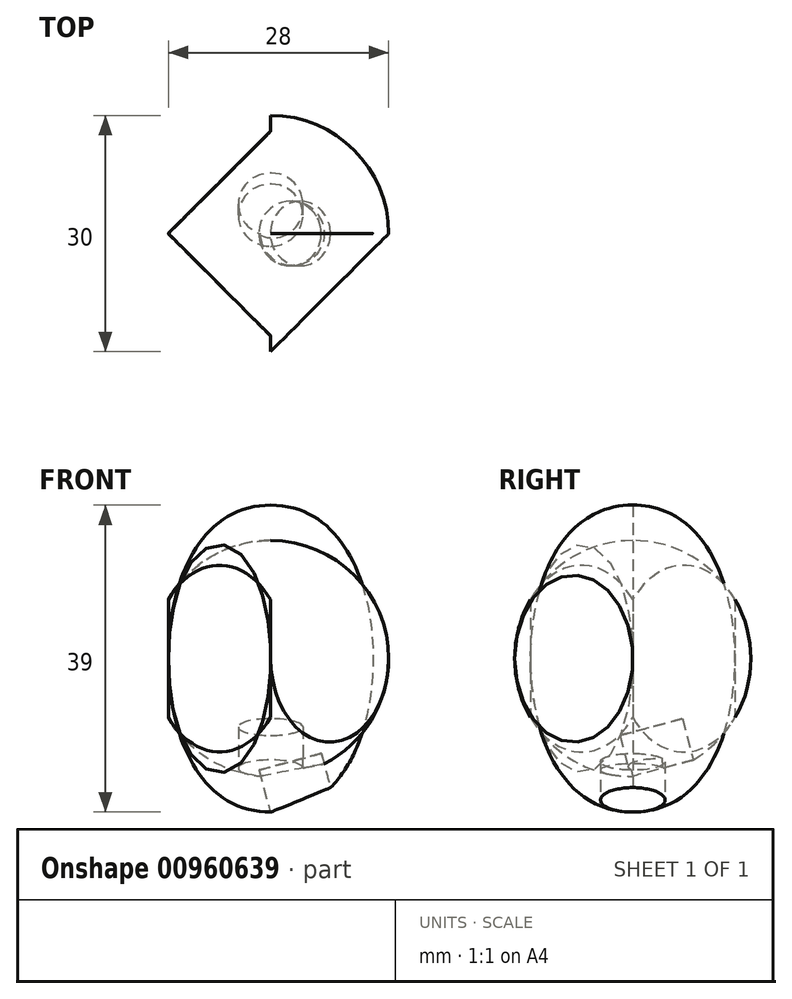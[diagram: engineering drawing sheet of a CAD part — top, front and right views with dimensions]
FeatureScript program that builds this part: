
annotation { "Feature Type Name" : "Feature", "Feature Type Description" : "" }
export const myFeature = defineFeature(function(context is Context, id is Id, definition is map)
    precondition{}
    {
        {
            var Q0;
            Q0=qCreatedBy(makeId("Front.planeOp"),FACE);
            var sketch = newSketch(context, id + "F0", { "sketchPlane" : qUnion([Q0])});
            skArc(sketch, "E0", {"start": v(0, -6) * mm, "mid": v(6, 0) * mm, "end": v(0, 6) * mm});
            skLineSegment(sketch, "E1", {"start": v(0, 6) * mm, "end": v(0, -6) * mm});
            skSolve(sketch);
        }
        {
            var Q0;
            Q0 = qSketchRegion(id + "F0", true);
            var Q1;
            Q1=sQuery(id+"F0.wireOp",EDGE,"E1");
            revolve(context, id + "F1", {"surfaceOperationType" : NewSurfaceOperationType.NEW, "entities" : qUnion([Q0]), "axis" : qUnion([Q1]), "revolveType" : RevolveType.FULL});
        }
        {
            var Q0;
            Q0=qCreatedBy(makeId("Front.planeOp"),FACE);
            var sketch = newSketch(context, id + "F2", { "sketchPlane" : qUnion([Q0])});
            skLineSegment(sketch, "E2", {"start": v(0, 16.05) * mm, "end": v(0, -21.63) * mm, "construction": true});
            skLineSegment(sketch, "E3.bottom", {"start": v(-1, 7.22) * mm, "end": v(1, 7.22) * mm});
            skLineSegment(sketch, "E3.top", {"start": v(-1, -7.38) * mm, "end": v(1, -7.38) * mm});
            skLineSegment(sketch, "E3.left", {"start": v(-1, 7.22) * mm, "end": v(-1, -7.38) * mm});
            skLineSegment(sketch, "E3.right", {"start": v(1, 7.22) * mm, "end": v(1, -7.38) * mm});
            skSolve(sketch);
        }
        {
            var Q0;
            Q0 = qSketchRegion(id + "F2", true);
            extrude(context, id + "F3", {"entities" : qUnion([Q0]), "operationType" : NewBodyOperationType.REMOVE, "endBound" : BoundingType.THROUGH_ALL, "oppositeDirection" : true, "depth" : 25 * mm, "offsetDistance" : 25 * mm, "hasSecondDirection" : true, "secondDirectionOppositeDirection" : false, "secondDirectionDepth" : 25 * mm});
        }
        {
            var Q0;
            Q0=qCreatedBy(makeId("Top.planeOp"),FACE);
            cPlane(context, id + "F4", {"entities" : qUnion([Q0]), "cplaneType" : CPlaneType.OFFSET, "offset" : 6 * mm, "width" : 150 * mm, "height" : 150 * mm});
        }
        {
            var Q0;
            Q0=qCreatedBy(id+"F4.planeOp",FACE);
            var sketch = newSketch(context, id + "F5", { "sketchPlane" : qUnion([Q0])});
            skLineSegment(sketch, "E4", {"start": v(-12.79, 0) * mm, "end": v(12.47, 0) * mm, "construction": true});
            skCircle(sketch, "E5", {"center": v(3.5, 0) * mm, "radius": 1.5 * mm});
            skCircle(sketch, "E6", {"center": v(-3.5, 0) * mm, "radius": 1.5 * mm});
            skSolve(sketch);
        }
        {
            var Q0;
            Q0 = qSketchRegion(id + "F5", true);
            extrude(context, id + "F6", {"entities" : qUnion([Q0]), "operationType" : NewBodyOperationType.REMOVE, "oppositeDirection" : true, "depth" : 6 * mm, "offsetDistance" : 25 * mm});
        }
        {
            var Q0;
            Q0=qCreatedBy(makeId("Front.planeOp"),FACE);
            var sketch = newSketch(context, id + "F7", { "sketchPlane" : qUnion([Q0])});
            skLineSegment(sketch, "E7.bottom", {"start": v(-12.5, 10) * mm, "end": v(12.5, 10) * mm, "construction": true});
            skLineSegment(sketch, "E7.top", {"start": v(-12.5, -10) * mm, "end": v(12.5, -10) * mm, "construction": true});
            skLineSegment(sketch, "E7.left", {"start": v(-12.5, 10) * mm, "end": v(-12.5, -10) * mm, "construction": true});
            skLineSegment(sketch, "E7.right", {"start": v(12.5, 10) * mm, "end": v(12.5, -10) * mm, "construction": true});
            skLineSegment(sketch, "E8", {"start": v(-15.17, 0) * mm, "end": v(15, 0) * mm, "construction": true});
            skPoint(sketch, "E9.snap10", {"position": v(0, 10) * mm});
            skFitSpline(sketch, "E10", {"points": [v(-12.5, 0) * mm, v(0, 10) * mm, v(12.5, 0) * mm], "startDerivative": vector(0, 35.85) * mm, "endDerivative": vector(0, -35.89) * mm});
            skLineSegment(sketch, "E11", {"start": v(-12.5, 0) * mm, "end": v(12.5, 0) * mm});
            skSolve(sketch);
        }
        {
            var Q0;
            Q0 = qSketchRegion(id + "F7", true);
            var Q1;
            Q1=sQuery(id+"F7.wireOp",EDGE,"E11");
            revolve(context, id + "F8", {"surfaceOperationType" : NewSurfaceOperationType.NEW, "entities" : qUnion([Q0]), "axis" : qUnion([Q1]), "revolveType" : RevolveType.FULL});
        }
        {
            var Q0;
            Q0=qCreatedBy(makeId("Front.planeOp"),FACE);
            var sketch = newSketch(context, id + "F9", { "sketchPlane" : qUnion([Q0])});
            skLineSegment(sketch, "E12.bottom", {"start": v(-19.8, 1) * mm, "end": v(19.67, 1) * mm});
            skLineSegment(sketch, "E12.top", {"start": v(-19.8, -1) * mm, "end": v(19.67, -1) * mm});
            skLineSegment(sketch, "E12.left", {"start": v(-19.8, 1) * mm, "end": v(-19.8, -1) * mm});
            skLineSegment(sketch, "E12.right", {"start": v(19.67, 1) * mm, "end": v(19.67, -1) * mm});
            skSolve(sketch);
        }
        {
            var Q0;
            Q0 = qSketchRegion(id + "F9", true);
            extrude(context, id + "F10", {"entities" : qUnion([Q0]), "operationType" : NewBodyOperationType.REMOVE, "endBound" : BoundingType.THROUGH_ALL, "oppositeDirection" : true, "depth" : 25 * mm, "offsetDistance" : 25 * mm, "hasSecondDirection" : true, "secondDirectionOppositeDirection" : false, "secondDirectionDepth" : 25 * mm});
        }
        {
            var Q0;
            Q0=qCreatedBy(makeId("Top.planeOp"),FACE);
            cPlane(context, id + "F11", {"entities" : qUnion([Q0]), "cplaneType" : CPlaneType.OFFSET, "offset" : 10 * mm, "width" : 150 * mm, "height" : 150 * mm});
        }
        {
            var Q0;
            Q0=qCreatedBy(id+"F11.planeOp",FACE);
            var sketch = newSketch(context, id + "F12", { "sketchPlane" : qUnion([Q0])});
            skLineSegment(sketch, "E13", {"start": v(-18, 0) * mm, "end": v(16.68, 0) * mm, "construction": true});
            skCircle(sketch, "E14", {"center": v(-6, 0) * mm, "radius": 1.5 * mm});
            skSolve(sketch);
        }
        {
            var Q0;
            Q0 = qSketchRegion(id + "F12", true);
            extrude(context, id + "F13", {"entities" : qUnion([Q0]), "operationType" : NewBodyOperationType.REMOVE, "oppositeDirection" : true, "depth" : 6 * mm, "offsetDistance" : 25 * mm});
        }
        {
            var Q0;
            Q0=makeQuery(id+"F3.boolean.opBoolean","SPLIT",BODY,{"disambiguationData":[OD(1.0)],"derivedFrom":makeQuery(id+"F1.opRevolve","SWEPT_BODY",BODY,{"disambiguationData":[OSD([sQuery(id+"F0.wireOp",EDGE,"E0"),sQuery(id+"F0.wireOp",EDGE,"E1")])]})});
            deleteBodies(context, id + "F14", {"entities" : qUnion([Q0])});
        }
        {
            var Q0;
            Q0=makeQuery(id+"F10.boolean.opBoolean","SPLIT",BODY,{"disambiguationData":[OD(1.0)],"derivedFrom":makeQuery(id+"F8.opRevolve","SWEPT_BODY",BODY,{"disambiguationData":[OSD([sQuery(id+"F7.wireOp",EDGE,"E10"),sQuery(id+"F7.wireOp",EDGE,"E11")])]})});
            deleteBodies(context, id + "F15", {"entities" : qUnion([Q0])});
        }
        {
            var Q0;
            Q0=qCreatedBy(makeId("Front.planeOp"),FACE);
            var sketch = newSketch(context, id + "F16", { "sketchPlane" : qUnion([Q0])});
            skArc(sketch, "E15", {"start": v(0, -15) * mm, "mid": v(15, 0) * mm, "end": v(0, 15) * mm});
            skLineSegment(sketch, "E16", {"start": v(0, 15) * mm, "end": v(0, -15) * mm});
            skSolve(sketch);
        }
        {
            var Q0;
            Q0 = qSketchRegion(id + "F16", true);
            var Q1;
            Q1=sQuery(id+"F16.wireOp",EDGE,"E16");
            revolve(context, id + "F17", {"surfaceOperationType" : NewSurfaceOperationType.NEW, "entities" : qUnion([Q0]), "axis" : qUnion([Q1]), "revolveType" : RevolveType.FULL});
        }
        {
            var Q0;
            Q0=qCreatedBy(makeId("Top.planeOp"),FACE);
            var sketch = newSketch(context, id + "F18", { "sketchPlane" : qUnion([Q0])});
            skLineSegment(sketch, "E17", {"start": v(0, 171.32) * mm, "end": v(0, -202.95) * mm, "construction": true});
            skLineSegment(sketch, "E18", {"start": v(-199.18, 0) * mm, "end": v(193.35, 0) * mm, "construction": true});
            skCircle(sketch, "E19", {"center": v(0, 0) * mm, "radius": 15 * mm, "construction": true});
            skLineSegment(sketch, "E20", {"start": v(-22.47, 0) * mm, "end": v(-15, 0) * mm});
            skLineSegment(sketch, "E21", {"start": v(-15, 0) * mm, "end": v(0, -15) * mm});
            skLineSegment(sketch, "E22", {"start": v(0, -15) * mm, "end": v(15, 0) * mm});
            skLineSegment(sketch, "E23", {"start": v(15, 0) * mm, "end": v(22.44, 0) * mm});
            skLineSegment(sketch, "E24", {"start": v(22.44, 0) * mm, "end": v(22.44, -21.7) * mm});
            skLineSegment(sketch, "E25", {"start": v(22.44, -21.7) * mm, "end": v(-22.47, -21.7) * mm});
            skLineSegment(sketch, "E26", {"start": v(-22.47, -21.7) * mm, "end": v(-22.47, 0) * mm});
            skSolve(sketch);
        }
        {
            var Q0;
            Q0 = qSketchRegion(id + "F18", true);
            extrude(context, id + "F19", {"entities" : qUnion([Q0]), "operationType" : NewBodyOperationType.REMOVE, "endBound" : BoundingType.THROUGH_ALL, "oppositeDirection" : true, "depth" : 25 * mm, "offsetDistance" : 25 * mm, "hasSecondDirection" : true, "secondDirectionOppositeDirection" : false, "secondDirectionDepth" : 25 * mm});
        }
        {
            var Q0;
            Q0=qCreatedBy(makeId("Right.planeOp"),FACE);
            var sketch = newSketch(context, id + "F20", { "sketchPlane" : qUnion([Q0])});
            skCircle(sketch, "E27", {"center": v(0, 0) * mm, "radius": 15 * mm, "construction": true});
            skLineSegment(sketch, "E28", {"start": v(-19.19, -20.67) * mm, "end": v(25.4, -8.72) * mm, "construction": true});
            skLineSegment(sketch, "E29", {"start": v(36.07, 0) * mm, "end": v(-35.32, 0) * mm, "construction": true});
            skLineSegment(sketch, "E30", {"start": v(0, 0) * mm, "end": v(8.49, -31.68) * mm, "construction": true});
            skSolve(sketch);
        }
        {
            var Q0;
            Q0=sQuery(id+"F20.wireOp",EDGE,"E28");
            cPlane(context, id + "F21", {"entities" : qUnion([Q0]), "cplaneType" : CPlaneType.LINE_ANGLE, "offset" : 25 * mm, "angle" : 0 * degree, "width" : 150 * mm, "height" : 150 * mm});
        }
        {
            var Q0;
            Q0=qCreatedBy(id+"F21.planeOp",FACE);
            var sketch = newSketch(context, id + "F22", { "sketchPlane" : qUnion([Q0])});
            skCircle(sketch, "E31", {"center": v(0, 0) * mm, "radius": 4.1 * mm});
            skSolve(sketch);
        }
        {
            var Q0;
            Q0 = qSketchRegion(id + "F22", true);
            extrude(context, id + "F23", {"entities" : qUnion([Q0]), "operationType" : NewBodyOperationType.REMOVE, "depth" : 6 * mm, "offsetDistance" : 25 * mm});
        }
        {
            var Q0;
            Q0=qCreatedBy(makeId("Front.planeOp"),FACE);
            var sketch = newSketch(context, id + "F24", { "sketchPlane" : qUnion([Q0])});
            skLineSegment(sketch, "E32.bottom", {"start": v(-13, 19.5) * mm, "end": v(13, 19.5) * mm, "construction": true});
            skLineSegment(sketch, "E32.top", {"start": v(-13, -19.5) * mm, "end": v(13, -19.5) * mm, "construction": true});
            skLineSegment(sketch, "E32.left", {"start": v(-13, 19.5) * mm, "end": v(-13, -19.5) * mm, "construction": true});
            skLineSegment(sketch, "E32.right", {"start": v(13, 19.5) * mm, "end": v(13, -19.5) * mm, "construction": true});
            skLineSegment(sketch, "E33", {"start": v(0, 23.39) * mm, "end": v(0, -22.69) * mm, "construction": true});
            skLineSegment(sketch, "E34", {"start": v(-15.9, 0) * mm, "end": v(17.34, 0) * mm, "construction": true});
            skPoint(sketch, "E34.endSnap0", {"position": v(13, 0) * mm});
            skFitSpline(sketch, "E35", {"points": [v(0, 19.5) * mm, v(13, 0) * mm, v(0, -19.5) * mm], "startDerivative": vector(54, 0) * mm, "endDerivative": vector(-54, 0) * mm});
            skLineSegment(sketch, "E36", {"start": v(9, 22.17) * mm, "end": v(9, -23.9) * mm, "construction": true});
            skLineSegment(sketch, "E37", {"start": v(0, 19.5) * mm, "end": v(0, -19.5) * mm});
            skSolve(sketch);
        }
        {
            var Q0;
            Q0 = qSketchRegion(id + "F24", true);
            var Q1;
            Q1=sQuery(id+"F24.wireOp",EDGE,"E37");
            revolve(context, id + "F25", {"surfaceOperationType" : NewSurfaceOperationType.NEW, "entities" : qUnion([Q0]), "axis" : qUnion([Q1]), "revolveType" : RevolveType.FULL});
        }
        {
            var Q0;
            Q0=qCreatedBy(makeId("Top.planeOp"),FACE);
            var sketch = newSketch(context, id + "F26", { "sketchPlane" : qUnion([Q0])});
            skCircle(sketch, "E38", {"center": v(0, 0) * mm, "radius": 13 * mm, "construction": true});
            skLineSegment(sketch, "E39", {"start": v(0, 17.25) * mm, "end": v(0, -15.41) * mm, "construction": true});
            skLineSegment(sketch, "E40", {"start": v(15.6, 0) * mm, "end": v(-15.87, 0) * mm, "construction": true});
            skLineSegment(sketch, "E41", {"start": v(0, 13) * mm, "end": v(-13, 0) * mm});
            skLineSegment(sketch, "E42", {"start": v(-13, 0) * mm, "end": v(0, -13) * mm});
            skLineSegment(sketch, "E43", {"start": v(0, -13) * mm, "end": v(0, -18.98) * mm});
            skLineSegment(sketch, "E44", {"start": v(0, -18.98) * mm, "end": v(-22.29, -20.73) * mm});
            skLineSegment(sketch, "E45", {"start": v(-22.29, -20.73) * mm, "end": v(-19.2, 18.67) * mm});
            skLineSegment(sketch, "E46", {"start": v(-19.2, 18.67) * mm, "end": v(0, 17.25) * mm});
            skLineSegment(sketch, "E47", {"start": v(0, 17.25) * mm, "end": v(0, 13) * mm});
            skSolve(sketch);
        }
        {
            var Q0;
            Q0 = qSketchRegion(id + "F26", true);
            extrude(context, id + "F27", {"entities" : qUnion([Q0]), "operationType" : NewBodyOperationType.REMOVE, "endBound" : BoundingType.THROUGH_ALL, "depth" : 25 * mm, "offsetDistance" : 25 * mm, "hasSecondDirection" : true, "secondDirectionOppositeDirection" : true, "secondDirectionDepth" : 25 * mm});
        }
        {
            var Q0;
            Q0=qCreatedBy(makeId("Front.planeOp"),FACE);
            var sketch = newSketch(context, id + "F28", { "sketchPlane" : qUnion([Q0])});
            skLineSegment(sketch, "E48", {"start": v(0, 22.73) * mm, "end": v(0, -30.09) * mm, "construction": true});
            skLineSegment(sketch, "E49", {"start": v(-4.15, -21.1) * mm, "end": v(30.9, -11.7) * mm, "construction": true});
            skSolve(sketch);
        }
        {
            var Q0;
            Q0=sQuery(id+"F28.wireOp",EDGE,"E49");
            cPlane(context, id + "F29", {"entities" : qUnion([Q0]), "cplaneType" : CPlaneType.LINE_ANGLE, "offset" : 25 * mm, "angle" : 90 * degree, "width" : 150 * mm, "height" : 150 * mm});
        }
        {
            var Q0;
            Q0=qCreatedBy(id+"F29.planeOp",FACE);
            var sketch = newSketch(context, id + "F30", { "sketchPlane" : qUnion([Q0])});
            skLineSegment(sketch, "E50", {"start": v(-15.46, 0) * mm, "end": v(18, 0) * mm, "construction": true});
            skCircle(sketch, "E51", {"center": v(-1, 0) * mm, "radius": 4.1 * mm});
            skSolve(sketch);
        }
        {
            var Q0;
            Q0 = qSketchRegion(id + "F30", true);
            extrude(context, id + "F31", {"entities" : qUnion([Q0]), "operationType" : NewBodyOperationType.REMOVE, "depth" : 6 * mm, "offsetDistance" : 25 * mm});
        }
    });
